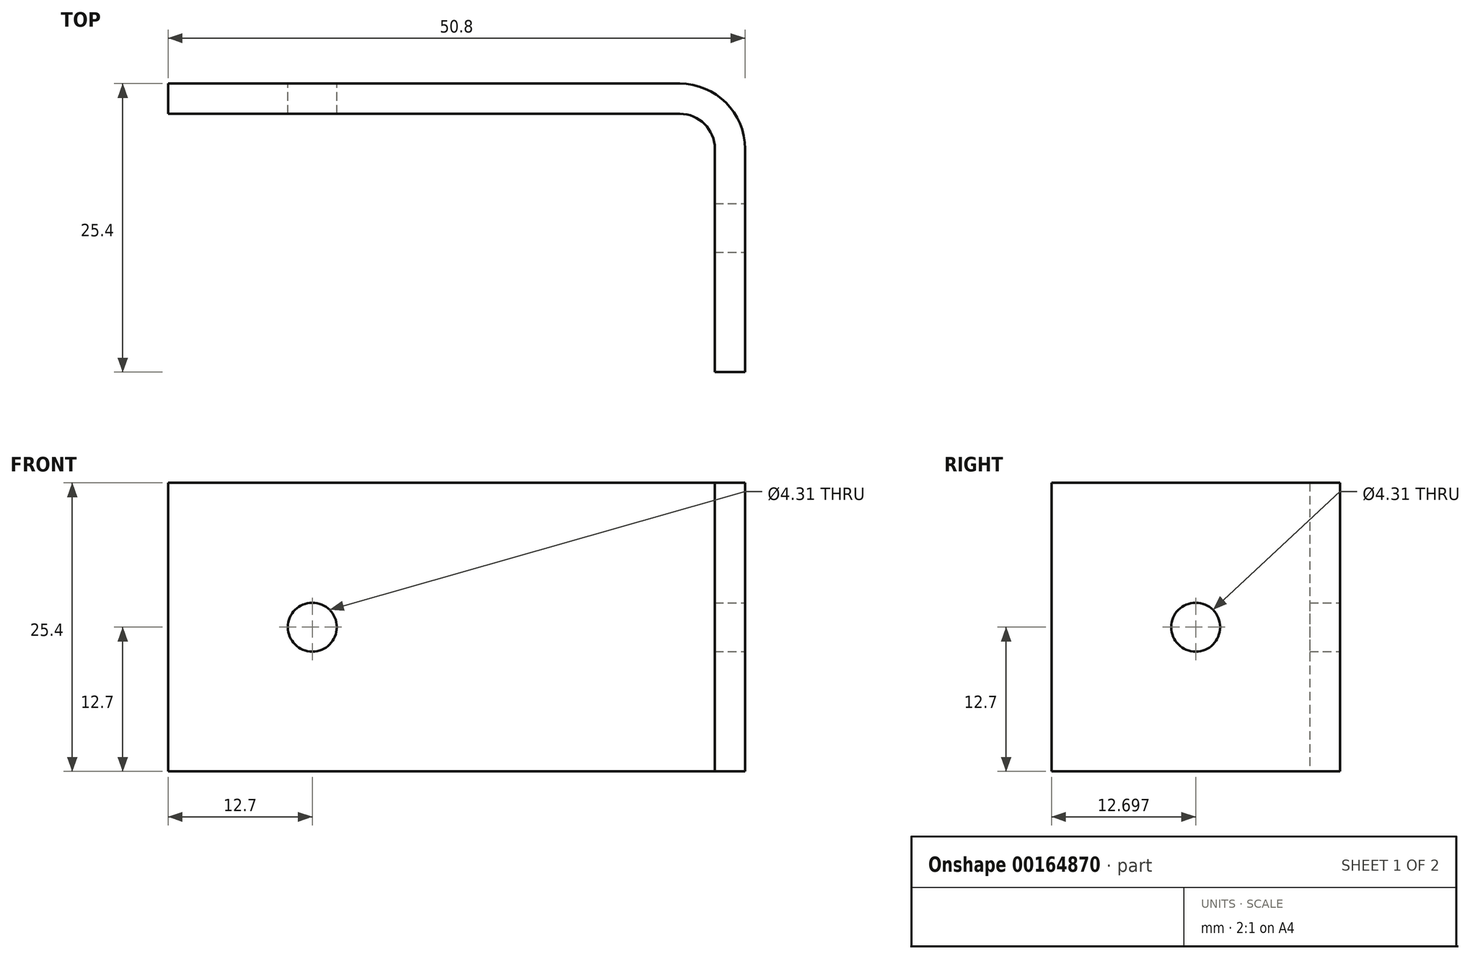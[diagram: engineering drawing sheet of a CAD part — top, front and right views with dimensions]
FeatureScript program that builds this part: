
annotation { "Feature Type Name" : "Feature", "Feature Type Description" : "" }
export const myFeature = defineFeature(function(context is Context, id is Id, definition is map)
    precondition{}
    {
        {
            var Q0;
            Q0=qCreatedBy(makeId("Top.planeOp"),FACE);
            var sketch = newSketch(context, id + "F0", { "sketchPlane" : qUnion([Q0])});
            skLineSegment(sketch, "E0.bottom", {"start": v(0, 0) * mm, "end": v(48.14, 0) * mm});
            skLineSegment(sketch, "E0.top", {"start": v(0, 2.66) * mm, "end": v(50.8, 2.66) * mm});
            skLineSegment(sketch, "E0.left", {"start": v(0, 0) * mm, "end": v(0, 2.66) * mm});
            skLineSegment(sketch, "E1.top", {"start": v(48.14, -22.74) * mm, "end": v(50.8, -22.74) * mm});
            skLineSegment(sketch, "E1.left", {"start": v(48.14, 0) * mm, "end": v(48.14, -22.74) * mm});
            skLineSegment(sketch, "E1.right", {"start": v(50.8, 2.66) * mm, "end": v(50.8, -22.74) * mm});
            skSolve(sketch);
        }
        {
            var Q0;
            Q0 = qSketchRegion(id + "F0", true);
            extrude(context, id + "F1", {"entities" : qUnion([Q0]), "depth" : 25.4 * mm});
        }
        {
            var Q0;
            Q0=makeQuery(id+"F1.opExtrude","SWEPT_FACE",FACE,{"disambiguationData":[OSD([sQuery(id+"F0.wireOp",EDGE,"E0.top")])]});
            var sketch = newSketch(context, id + "F2", { "sketchPlane" : qUnion([Q0])});
            skLineSegment(sketch, "E2.bottom", {"start": v(0, 12.7) * mm, "end": v(-12.7, 12.7) * mm, "construction": true});
            skLineSegment(sketch, "E2.top", {"start": v(0, 25.4) * mm, "end": v(-12.7, 25.4) * mm, "construction": true});
            skLineSegment(sketch, "E2.left", {"start": v(0, 12.7) * mm, "end": v(0, 25.4) * mm, "construction": true});
            skLineSegment(sketch, "E2.right", {"start": v(-12.7, 12.7) * mm, "end": v(-12.7, 25.4) * mm, "construction": true});
            skCircle(sketch, "E3", {"center": v(-12.7, 12.7) * mm, "radius": 2.15 * mm});
            skSolve(sketch);
        }
        {
            var Q0;
            Q0 = qSketchRegion(id + "F2", true);
            var Q1;
            Q1=makeQuery(id+"F1.opExtrude","SWEPT_FACE",FACE,{"disambiguationData":[OSD([sQuery(id+"F0.wireOp",EDGE,"E0.bottom")])]});
            extrude(context, id + "F3", {"entities" : qUnion([Q0]), "operationType" : NewBodyOperationType.REMOVE, "endBound" : BoundingType.UP_TO_SURFACE, "oppositeDirection" : true, "endBoundEntityFace" : qUnion([Q1]), "depth" : 25.4 * mm});
        }
        {
            var Q0;
            Q0=makeQuery(id+"F1.opExtrude","SWEPT_FACE",FACE,{"disambiguationData":[OSD([sQuery(id+"F0.wireOp",EDGE,"E1.right")])]});
            var sketch = newSketch(context, id + "F4", { "sketchPlane" : qUnion([Q0])});
            skLineSegment(sketch, "E4.bottom", {"start": v(-22.74, 12.7) * mm, "end": v(-10.04, 12.7) * mm, "construction": true});
            skLineSegment(sketch, "E4.top", {"start": v(-22.74, 25.4) * mm, "end": v(-10.04, 25.4) * mm, "construction": true});
            skLineSegment(sketch, "E4.left", {"start": v(-22.74, 12.7) * mm, "end": v(-22.74, 25.4) * mm, "construction": true});
            skLineSegment(sketch, "E4.right", {"start": v(-10.04, 12.7) * mm, "end": v(-10.04, 25.4) * mm, "construction": true});
            skCircle(sketch, "E5", {"center": v(-10.04, 12.7) * mm, "radius": 2.15 * mm});
            skSolve(sketch);
        }
        {
            var Q0;
            Q0 = qSketchRegion(id + "F4", true);
            var Q1;
            Q1=makeQuery(id+"F1.opExtrude","SWEPT_FACE",FACE,{"disambiguationData":[OSD([sQuery(id+"F0.wireOp",EDGE,"E1.left")])]});
            extrude(context, id + "F5", {"entities" : qUnion([Q0]), "operationType" : NewBodyOperationType.REMOVE, "endBound" : BoundingType.UP_TO_SURFACE, "oppositeDirection" : true, "endBoundEntityFace" : qUnion([Q1]), "depth" : 25.4 * mm});
        }
        {
            var Q0;
            Q0=makeQuery(id+"F1.opExtrude","SWEPT_EDGE",EDGE,{"disambiguationData":[OSD([sQuery(id+"F0.wireOp",EDGE,"E0.bottom"),sQuery(id+"F0.wireOp",EDGE,"E1.left")])]});
            fillet(context, id + "F6", {"entities" : qUnion([Q0]), "radius" : 3.08 * mm, "tangentPropagation" : true, "allowEdgeOverflow" : false});
        }
        {
            var Q0;
            Q0=makeQuery(id+"F1.opExtrude","SWEPT_EDGE",EDGE,{"disambiguationData":[OSD([sQuery(id+"F0.wireOp",EDGE,"E0.top"),sQuery(id+"F0.wireOp",EDGE,"E1.right")])]});
            fillet(context, id + "F7", {"entities" : qUnion([Q0]), "radius" : 5.74 * mm, "tangentPropagation" : true, "allowEdgeOverflow" : false});
        }
    });
